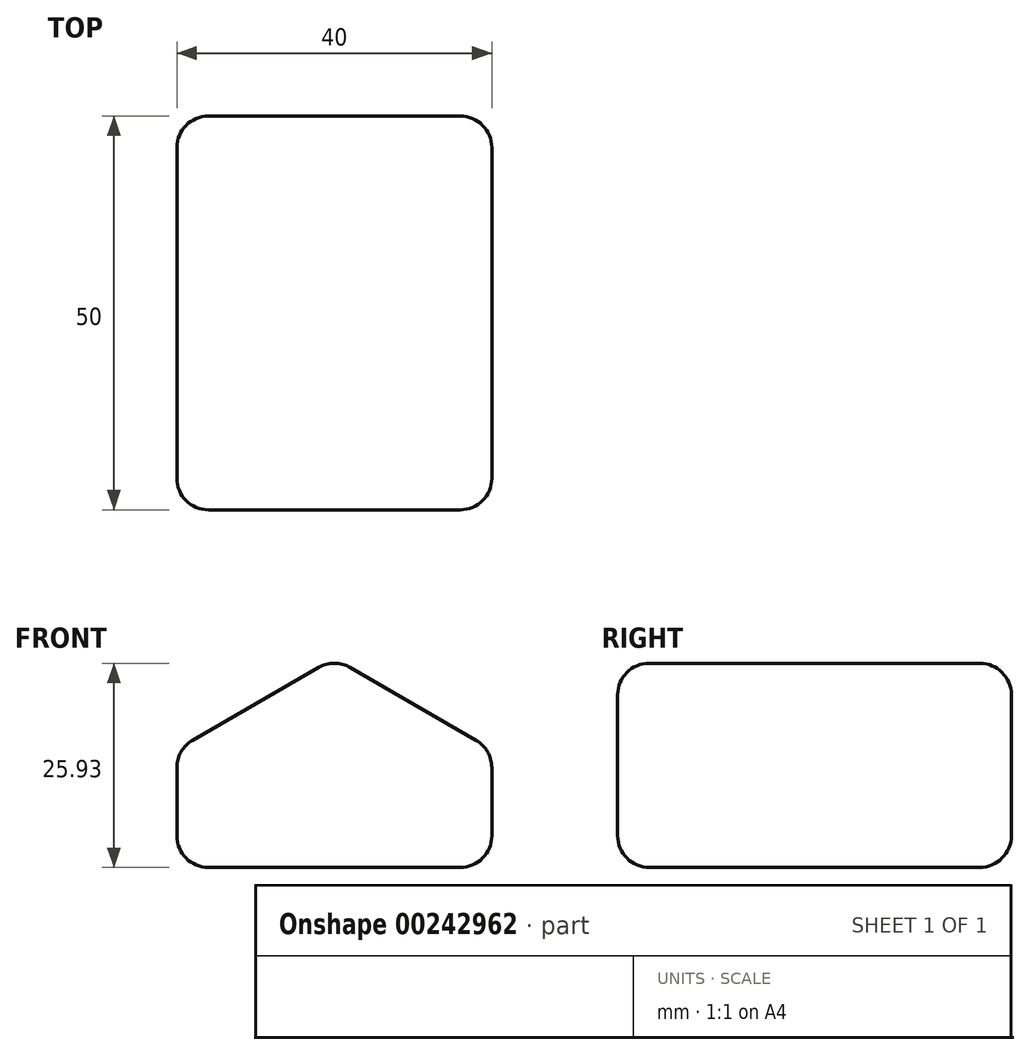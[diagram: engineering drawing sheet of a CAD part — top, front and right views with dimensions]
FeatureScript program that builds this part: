
annotation { "Feature Type Name" : "Feature", "Feature Type Description" : "" }
export const myFeature = defineFeature(function(context is Context, id is Id, definition is map)
    precondition{}
    {
        {
            var Q0;
            Q0=qCreatedBy(makeId("Front.planeOp"),FACE);
            var sketch = newSketch(context, id + "F0", { "sketchPlane" : qUnion([Q0])});
            skLineSegment(sketch, "E0", {"start": v(0, 0) * mm, "end": v(20, 0) * mm});
            skLineSegment(sketch, "E1", {"start": v(20, 0) * mm, "end": v(20, 15) * mm});
            skLineSegment(sketch, "E2", {"start": v(20, 15) * mm, "end": v(0, 26.55) * mm});
            skLineSegment(sketch, "E3", {"start": v(0, 26.55) * mm, "end": v(-20, 15) * mm});
            skLineSegment(sketch, "E4", {"start": v(-20, 15) * mm, "end": v(-20, 0) * mm});
            skLineSegment(sketch, "E5", {"start": v(-20, 0) * mm, "end": v(0, 0) * mm});
            skLineSegment(sketch, "E6", {"start": v(0, 26.55) * mm, "end": v(0, 0) * mm, "construction": true});
            skLineSegment(sketch, "E7", {"start": v(-20, 15) * mm, "end": v(0, 15) * mm, "construction": true});
            skSolve(sketch);
        }
        {
            var Q0;
            Q0 = qSketchRegion(id + "F0", true);
            extrude(context, id + "F1", {"entities" : qUnion([Q0]), "endBound" : BoundingType.SYMMETRIC, "depth" : 50 * mm});
        }
        {
            var Q0;
            Q0=makeQuery(id+"F1.opExtrude","CAP_EDGE",EDGE,{"disambiguationData":[OSD([sQuery(id+"F0.wireOp",EDGE,"E2")])],"isStart":false});
            var Q1;
            Q1=makeQuery(id+"F1.opExtrude","CAP_EDGE",EDGE,{"disambiguationData":[OSD([sQuery(id+"F0.wireOp",EDGE,"E3")])],"isStart":false});
            var Q2;
            Q2=makeQuery(id+"F1.opExtrude","CAP_FACE",FACE,{"disambiguationData":[OSD([sQuery(id+"F0.wireOp",EDGE,"E0"),sQuery(id+"F0.wireOp",EDGE,"E1"),sQuery(id+"F0.wireOp",EDGE,"E2"),sQuery(id+"F0.wireOp",EDGE,"E3"),sQuery(id+"F0.wireOp",EDGE,"E4"),sQuery(id+"F0.wireOp",EDGE,"E5")])],"isStart":false});
            var Q3;
            Q3=makeQuery(id+"F1.opExtrude","CAP_FACE",FACE,{"disambiguationData":[OSD([sQuery(id+"F0.wireOp",EDGE,"E0"),sQuery(id+"F0.wireOp",EDGE,"E1"),sQuery(id+"F0.wireOp",EDGE,"E2"),sQuery(id+"F0.wireOp",EDGE,"E3"),sQuery(id+"F0.wireOp",EDGE,"E4"),sQuery(id+"F0.wireOp",EDGE,"E5")])],"isStart":true});
            var Q4;
            Q4=makeQuery(id+"F1.opExtrude","SWEPT_FACE",FACE,{"disambiguationData":[OSD([sQuery(id+"F0.wireOp",EDGE,"E1")])]});
            var Q5;
            Q5=makeQuery(id+"F1.opExtrude","SWEPT_FACE",FACE,{"disambiguationData":[OSD([sQuery(id+"F0.wireOp",EDGE,"E2")])]});
            var Q6;
            Q6=makeQuery(id+"F1.opExtrude","SWEPT_FACE",FACE,{"disambiguationData":[OSD([sQuery(id+"F0.wireOp",EDGE,"E4")])]});
            var Q7;
            Q7=makeQuery(id+"F1.opExtrude","SWEPT_FACE",FACE,{"disambiguationData":[OSD([sQuery(id+"F0.wireOp",EDGE,"E3")])]});
            fillet(context, id + "F2", {"entities" : qUnion([Q0, Q1, Q2, Q3, Q4, Q5, Q6, Q7]), "radius" : 4 * mm, "tangentPropagation" : true, "allowEdgeOverflow" : false});
        }
    });
